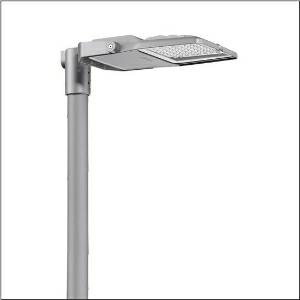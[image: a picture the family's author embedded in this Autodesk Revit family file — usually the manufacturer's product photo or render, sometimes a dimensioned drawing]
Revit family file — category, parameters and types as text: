
# Revit family: floodlight_fl_21_iq_mini___pl52_5xa7771c4d3a_e4a2
name_source: partatom
category: Lighting Fixtures
units: mm (PartAtom-declared; Revit-internal decimal feet)

## family parameters
Cut with Voids When Loaded = No
Host = Face
Light Source = No
Part Type = Normal
Room Calculation Point = No
Round Connector Dimension = Use Diameter
Shared = No

## types (1)
- --- (1 x LED, 12720 lm, 87.2 W, 4000K)
    Apparent Load = 87 VA
    CIE Flux Codes = 26 60 98 100 100
    Color Rendering = 70
    Color Temperature = 4000K
    Default Elevation = 1800 mm
    Description = Floodlight FL 21 iQ mini, floodlight, primary light control with lens, of PMMA, primary optical cover: protective disc, of toughened safety glass, transparent, light distribution: PL52, light emission: direct distribution, installation type: surface-mounted, lamps: LED, High Power LED, rated values: 12.720lm | 87,2W | 145,9lm/W (begin service life); end service life: 12.720lm | 92,1W; at 50% lumin. flux: 6.360lm | 40,2W | 158,2lm/W, colour temperature: 4000K, colour rendering: CRI > 70, light colour: 740, light setting 1 begin service life: 100% | 12.720lm | 87,2W | 145,9lm/W | 4.000K, light setting 1 end service life: 92,1W, further light settings possible, control: Auto-Match, Temp-Guard, Lumen-Switch, Night-Set, Smart-Wire, Light-Fading, Desk-Remote (wireless, voltage-free reading and setting of iQ features in the workshop via application-optimized NFC function/RFID function), optimised constant luminous flux control (CLO 2.0), pre-setting: linear dimming characteristic, with terminal, 6-pole, mains connection: 220..240V, AC, 50/60Hz, luminaire housing, of diecast aluminium, powder-coated, SITECO metallic grey (DB 702S), corrosivity category C5 mid according to DIN EN ISO 12944suitable for swimming poolschlorine-resistant, sealing non-destructively replaceable, please order mast flange separately, mast bracket, of steel, galvanised, powder-coated, SITECO metallic grey (DB 702S), protection rating (complete): IP66, insulation class (complete): insulation class II (safety insulation), certification: CE, ENEC, VDE, protection symbol: D, impact resistance: IK08, permissible operating ambient temperature: -40..+40°C, permissible operating ambient temperature for outdoor applications: -40..+50°C, standard: DIN EN 12944, LABS conformity tested according to VDMA 24364:2018-05, packaging unit: 1 piece

Light Distribution: PL52
    Height = 70 mm
    Lamp = 1 x LED
    Lamp Light Flux = 12720 lm
    Lamp Power = 87.2 W
    Lamp count = 1
    Length = 485 mm
    Luminous efficacy = 146 lm/W
    Manufacturer = Siteco
    ModVariant = No
    Model = 5XA7771C4D3A
    Number of Poles = 1
    OnlyDefault = Yes
    Power Factor = 1
    Product Name = Floodlight FL 21 iQ mini | PL52
    Product group = floodlight | pylon annexe
    ProductGroupID = 6201
    Protection Class = Protection class II
    Protection Degree = IP 66
    RLX_Detail_Level = 1
    RLX_Emergency_Light_Flux = 0 lm
    RLX_Emergency_Type = 0
    RLX_Emergency_Type_DB = No
    RlxData = <blob elided: 101737 chars, md5=0489c004>
    Socket = socket
    Standby Power = 0 W
    System Light Flux = 12720 lm
    System Power = 87 W
    Type Comments = factory setting: luminous flux: 100 % | dim-lin: 254 | 456 mA
    Type Image = l_1007125.jpg
    URL = http://relux.com
    VarID = @adj_163917
    Voltage = 0 V
    Weight = 0.00 kg
    Width = 337 mm

## geometry (parser evidence)
native form markers: Blend x4, Sweep x11
no freeform markers — native parametric forms only
